# Revit family: K12.2 - Yoke Mount
name_source: partatom
category: Generic Models
revit_build: Autodesk Revit 2017 (Build: 20190508_0315(x64)
units: mm (PartAtom-declared; Revit-internal decimal feet)

## family parameters
Can host rebar = No
Cut with Voids When Loaded = No
Host = Face
Part Type = Normal
Room Calculation Point = No
Round Connector Dimension = Use Diameter
Shared = No

## types (4) — shared parameters
Coverage Horizontal = 75.00°
Coverage Vertical = 75.00°
Depth = 350 mm
Description = Multi-purpose, 2-way active loudspeaker
Height = 602 mm
Manufacturer = QSC, LLC
Manufacturer URL = www.qsc.com
Mount Depth = 401 mm
Mount Width = 115 mm
Product Documentation Link = https://www.qsc.com
Product Page URL = https://www.qsc.com
Regulatory Compliance = CE, RAEE, UL, China RoHS, RoHS II, FCC Class B
SPL Max = 132
Width = 356 mm
zero-valued in all types: Default Elevation

## per-type parameters (varying)
| type | End Pivot Speaker Distance From Mount | Model | Outer Yoke Width | Show End Pivot Model | Show Side Pivot Model | Side Pivot Speaker Distance From Mount | Weight Dimensional (kg) | Weight Dimensional (lb) | Weight Product (kg) | Weight Product (lb) |
| Side-Pivot, Furthest Position | 365 mm | K10.2 | 380 mm | No | Yes | 365 mm | 17.6 | 38.8 | 14.5 | 32 |
| Side-Pivot, Nearest Position | 265 mm | K12.2 | 380 mm | No | Yes | 302 mm | 21.7 | 47.8 | 17.7 | 39 |
| End-Pivot, Furthest Position | 365 mm | K12.2 | 650 mm  [stored 2.13255 ft] | Yes | No | 365 mm | 21.7 | 47.8 | 17.7 | 39 |
| End-Pivot, Nearest Position | 302 mm | K12.2 | 650 mm  [stored 2.13255 ft] | Yes | No | 302 mm | 47.8 | 21.7 | 17.7 | 39 |

note: [stored X ft] marks values corroborated as IEEE doubles in the binary element streams (Revit-internal decimal feet)

## geometry (parser evidence)
native form markers: Blend x4, Sweep x11
no freeform markers — native parametric forms only
